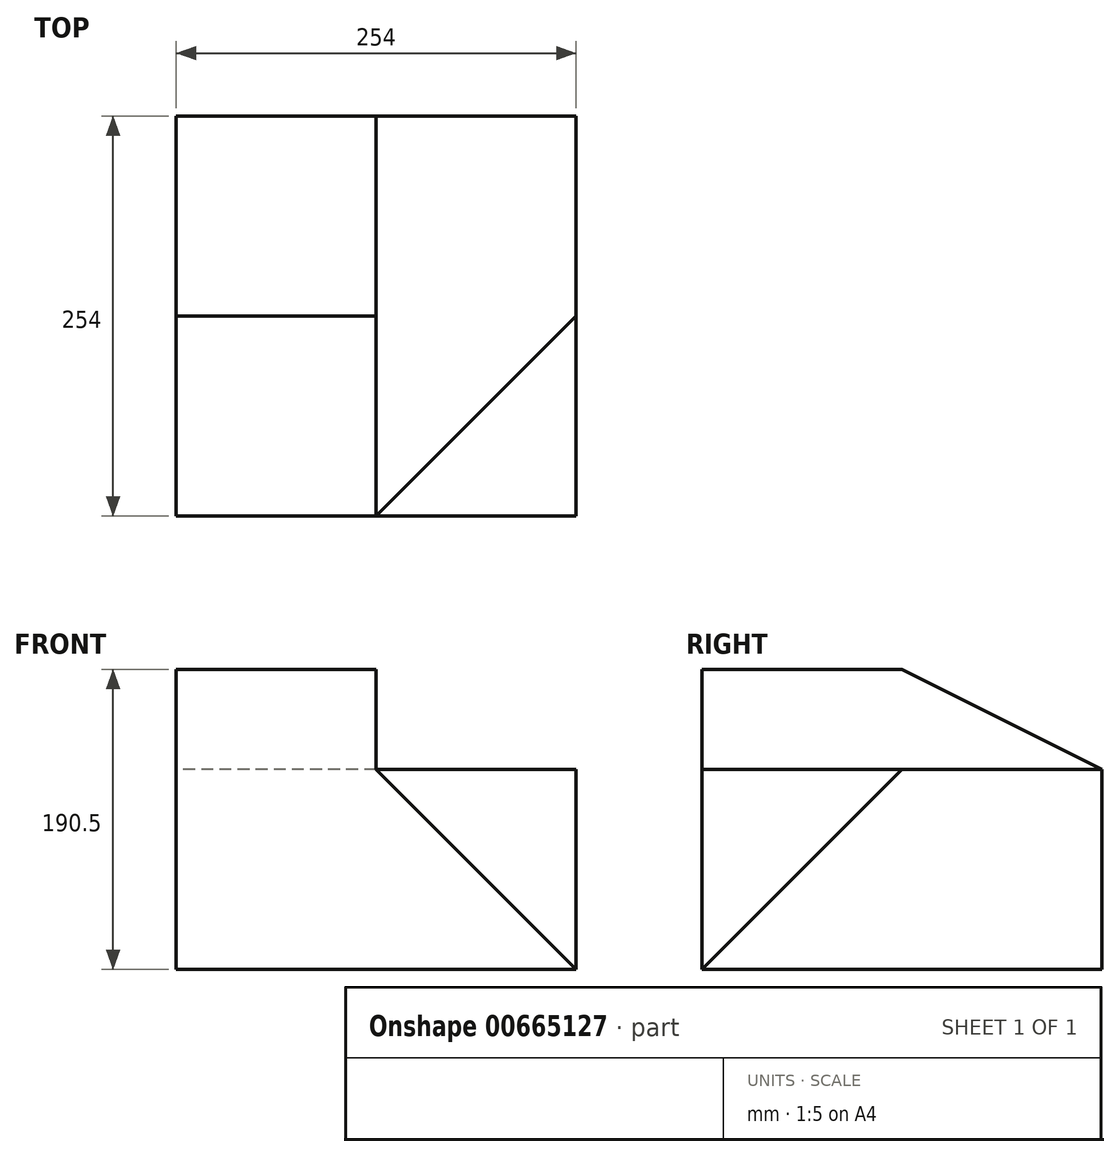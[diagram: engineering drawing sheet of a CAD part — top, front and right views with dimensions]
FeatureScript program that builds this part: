
annotation { "Feature Type Name" : "Feature", "Feature Type Description" : "" }
export const myFeature = defineFeature(function(context is Context, id is Id, definition is map)
    precondition{}
    {
        {
            var Q0;
            Q0=qCreatedBy(makeId("Right.planeOp"),FACE);
            var sketch = newSketch(context, id + "F0", { "sketchPlane" : qUnion([Q0])});
            skLineSegment(sketch, "E0", {"start": v(0, 0) * mm, "end": v(254, 0) * mm});
            skLineSegment(sketch, "E1", {"start": v(254, 0) * mm, "end": v(254, 127) * mm});
            skLineSegment(sketch, "E2", {"start": v(0, 0) * mm, "end": v(0, 127) * mm});
            skLineSegment(sketch, "E3", {"start": v(0, 127) * mm, "end": v(0, 190.5) * mm});
            skLineSegment(sketch, "E4", {"start": v(0, 190.5) * mm, "end": v(127, 190.5) * mm});
            skLineSegment(sketch, "E5", {"start": v(127, 190.5) * mm, "end": v(254, 127) * mm});
            skLineSegment(sketch, "E6", {"start": v(0, 127) * mm, "end": v(254, 127) * mm});
            skSolve(sketch);
        }
        {
            var Q0;
            Q0=makeQuery(id+"F0.imprint","IMPRINT",FACE,{"disambiguationData":[TD([[makeQuery(id+"F0.imprint","IMPRINT",EDGE,{"derivedFrom":sQuery(id+"F0.wireOp",EDGE,"E0")}),1.0]])]});
            var Q1;
            Q1=makeQuery(id+"F0.imprint","IMPRINT",FACE,{"disambiguationData":[TD([[makeQuery(id+"F0.imprint","IMPRINT",EDGE,{"derivedFrom":sQuery(id+"F0.wireOp",EDGE,"E2")}),-1.0]])]});
            extrude(context, id + "F1", {"entities" : qUnion([Q0, Q1]), "depth" : 254 * mm, "offsetDistance" : 25.4 * mm});
        }
        {
            var Q0;
            Q0=makeQuery(id+"F0.imprint","IMPRINT",FACE,{"disambiguationData":[TD([[makeQuery(id+"F0.imprint","IMPRINT",EDGE,{"derivedFrom":sQuery(id+"F0.wireOp",EDGE,"E3")}),-1.0]])]});
            extrude(context, id + "F2", {"entities" : qUnion([Q0]), "operationType" : NewBodyOperationType.ADD, "depth" : 127 * mm, "offsetDistance" : 25.4 * mm});
        }
        {
            var Q0;
            Q0=makeQuery(id+"F1.opExtrude","CAP_EDGE",EDGE,{"disambiguationData":[OSD([sQuery(id+"F0.wireOp",EDGE,"E6")])],"isStart":false});
            cPoint(context, id + "F3", {"entities" : qUnion([Q0]), "parameter" : 0.5});
        }
        {
            var Q0;
            Q0=makeQuery(id+"F1.opExtrude","CAP_VERTEX",VERTEX,{"disambiguationData":[OSD([sQuery(id+"F0.wireOp",EDGE,"E0"),sQuery(id+"F0.wireOp",EDGE,"E2"),sQuery(id+"F0.wireOp",EDGE,"yS0n7d75-RFB7-Cc18-eG3L-7raJqwCRv1EQ")])],"isStart":false});
            var Q1;
            Q1=makeQuery(id+"F2.opExtrude","CAP_VERTEX",VERTEX,{"disambiguationData":[OSD([sQuery(id+"F0.wireOp",EDGE,"E2"),sQuery(id+"F0.wireOp",EDGE,"6s2I8fPQ-ZTXl-qR3a-GZPI-27kgQpKXZmSV"),sQuery(id+"F0.wireOp",EDGE,"E3")])],"isStart":false});
            var Q2;
            Q2 = qCreatedBy(id + "F3" ,VERTEX);
            cPlane(context, id + "F4", {"entities" : qUnion([Q0, Q1, Q2]), "cplaneType" : CPlaneType.THREE_POINT, "offset" : 25.4 * mm, "width" : 152.4 * mm, "height" : 152.4 * mm});
        }
        {
            var Q0;
            Q0=qCreatedBy(id+"F4.planeOp",FACE);
            var sketch = newSketch(context, id + "F5", { "sketchPlane" : qUnion([Q0])});
            skLineSegment(sketch, "E7", {"start": v(207.4, 179.6) * mm, "end": v(51.85, 89.8) * mm});
            skLineSegment(sketch, "E8", {"start": v(207.4, 0) * mm, "end": v(207.4, 179.6) * mm});
            skLineSegment(sketch, "E9", {"start": v(51.85, 89.8) * mm, "end": v(207.4, 0) * mm});
            skLineSegment(sketch, "E10", {"start": v(-25.92, 134.7) * mm, "end": v(51.85, 89.8) * mm});
            skSolve(sketch);
        }
        {
            var Q0;
            Q0=makeQuery(id+"F5.imprint","IMPRINT",FACE,{"disambiguationData":[TD([[makeQuery(id+"F5.imprint","IMPRINT",EDGE,{"derivedFrom":sQuery(id+"F5.wireOp",EDGE,"E7")}),1.0]])]});
            extrude(context, id + "F6", {"entities" : qUnion([Q0]), "operationType" : NewBodyOperationType.REMOVE, "endBound" : BoundingType.THROUGH_ALL, "depth" : 25.4 * mm, "offsetDistance" : 25.4 * mm});
        }
    });
